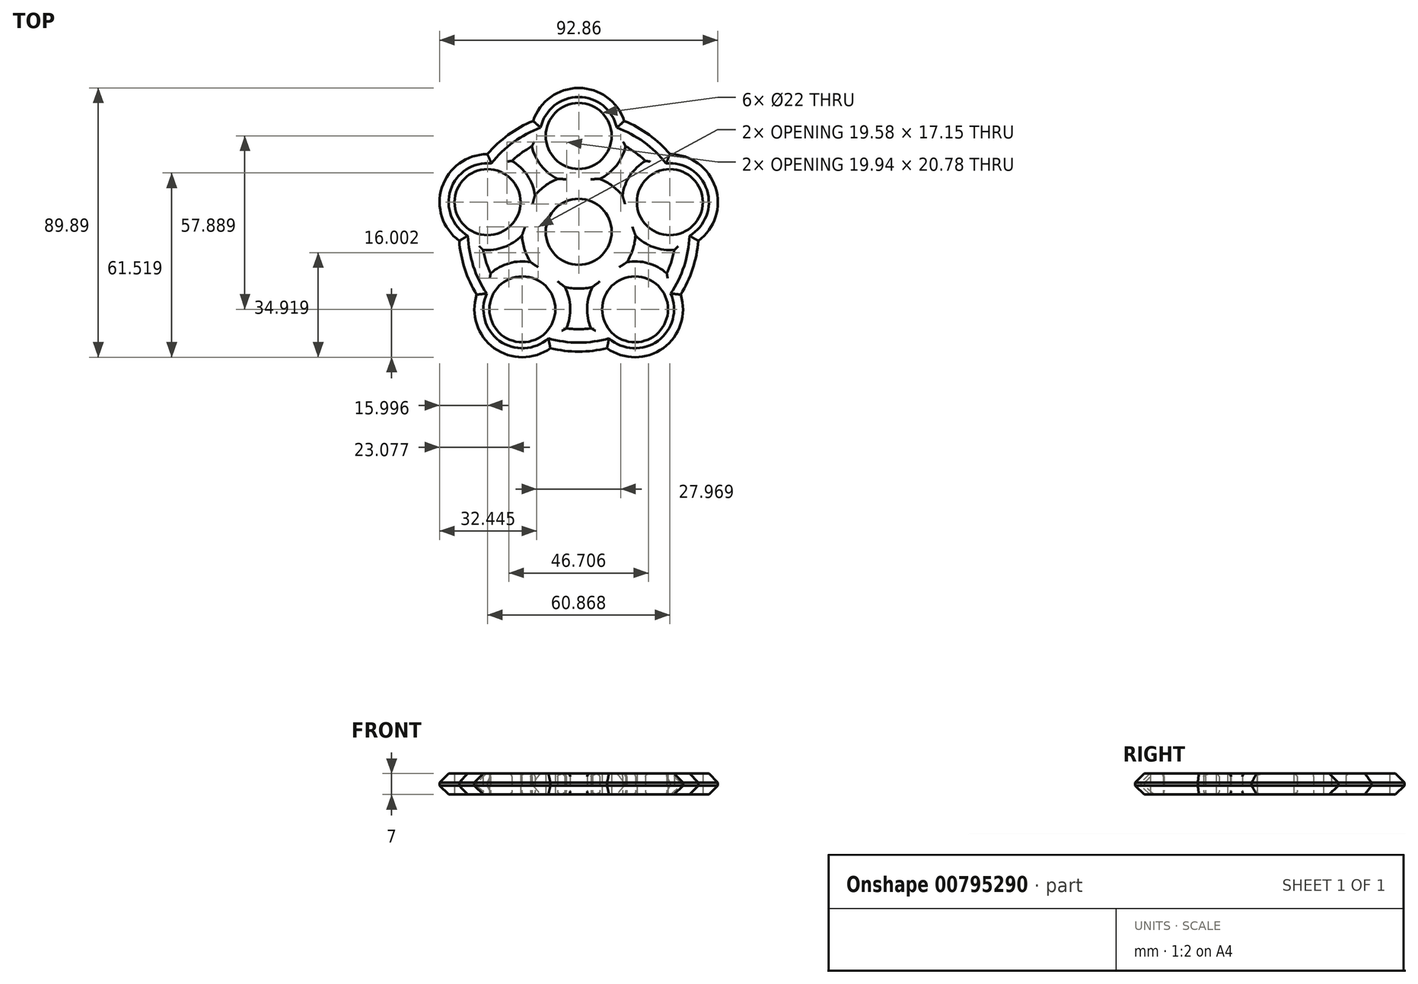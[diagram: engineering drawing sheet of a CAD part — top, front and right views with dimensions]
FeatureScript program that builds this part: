
annotation { "Feature Type Name" : "Feature", "Feature Type Description" : "" }
export const myFeature = defineFeature(function(context is Context, id is Id, definition is map)
    precondition{}
    {
        {
            var Q0;
            Q0=qCreatedBy(makeId("Top.planeOp"),FACE);
            var sketch = newSketch(context, id + "F0", { "sketchPlane" : qUnion([Q0])});
            skCircle(sketch, "E0", {"center": v(0, 0) * mm, "radius": 11 * mm});
            skCircle(sketch, "E1", {"center": v(0, 0) * mm, "radius": 19 * mm});
            skCircle(sketch, "E2", {"center": v(0, 0) * mm, "radius": 40 * mm});
            skCircle(sketch, "E3", {"center": v(0, 0) * mm, "radius": 32.5 * mm});
            skCircle(sketch, "E4", {"center": v(0, 32) * mm, "radius": 11 * mm});
            skCircle(sketch, "E5", {"center": v(0, 32) * mm, "radius": 16 * mm});
            skCircle(sketch, "E6.1.0", {"center": v(-30.43, 9.89) * mm, "radius": 16 * mm});
            skCircle(sketch, "E6.1.1", {"center": v(-30.43, 9.89) * mm, "radius": 11 * mm});
            skCircle(sketch, "E6.2.0", {"center": v(-18.8, -25.89) * mm, "radius": 16 * mm});
            skCircle(sketch, "E6.2.1", {"center": v(-18.8, -25.89) * mm, "radius": 11 * mm});
            skCircle(sketch, "E7.1.3.0", {"center": v(18.8, -25.89) * mm, "radius": 16 * mm});
            skCircle(sketch, "E7.2.3.0", {"center": v(18.8, -25.89) * mm, "radius": 11 * mm});
            skCircle(sketch, "E7.1.4.0", {"center": v(30.43, 9.89) * mm, "radius": 16 * mm});
            skCircle(sketch, "E7.2.4.0", {"center": v(30.43, 9.89) * mm, "radius": 11 * mm});
            skSolve(sketch);
        }
        {
            var Q0;
            {var subQ0=sQuery(id+"F0.wireOp",EDGE,"E6.1.0");var subQ1=sQuery(id+"F0.wireOp",EDGE,"E2");var subQ2=makeQuery(id+"F0.imprint","INTERSECT",VERTEX,{"disambiguationData":[OD(0.0)],"derivedFrom":[subQ1,subQ0]});Q0=makeQuery(id+"F0.imprint","IMPRINT",FACE,{"disambiguationData":[TD([[makeQuery(id+"F0.imprint","IMPRINT",EDGE,{"disambiguationData":[TD([[subQ2,-1.0]])],"derivedFrom":subQ1}),1.0]])]});}
            var Q1;
            {var subQ0=sQuery(id+"F0.wireOp",EDGE,"E6.1.0");var subQ1=sQuery(id+"F0.wireOp",EDGE,"E2");var subQ2=makeQuery(id+"F0.imprint","INTERSECT",VERTEX,{"disambiguationData":[OD(1.0)],"derivedFrom":[subQ1,subQ0]});Q1=makeQuery(id+"F0.imprint","IMPRINT",FACE,{"disambiguationData":[TD([[makeQuery(id+"F0.imprint","IMPRINT",EDGE,{"disambiguationData":[TD([[subQ2,1.0]])],"derivedFrom":subQ1}),1.0]])]});}
            var Q2;
            {var subQ0=sQuery(id+"F0.wireOp",EDGE,"E6.1.0");var subQ1=sQuery(id+"F0.wireOp",EDGE,"E2");var subQ2=makeQuery(id+"F0.imprint","INTERSECT",VERTEX,{"disambiguationData":[OD(1.0)],"derivedFrom":[subQ1,subQ0]});Q2=makeQuery(id+"F0.imprint","IMPRINT",FACE,{"disambiguationData":[TD([[makeQuery(id+"F0.imprint","IMPRINT",EDGE,{"disambiguationData":[TD([[subQ2,-1.0]])],"derivedFrom":subQ1}),1.0]])]});}
            var Q3;
            {var subQ0=sQuery(id+"F0.wireOp",EDGE,"E6.1.0");var subQ1=sQuery(id+"F0.wireOp",EDGE,"E2");var subQ2=makeQuery(id+"F0.imprint","INTERSECT",VERTEX,{"disambiguationData":[OD(0.0)],"derivedFrom":[subQ1,subQ0]});Q3=makeQuery(id+"F0.imprint","IMPRINT",FACE,{"disambiguationData":[TD([[makeQuery(id+"F0.imprint","IMPRINT",EDGE,{"disambiguationData":[TD([[subQ2,-1.0]])],"derivedFrom":subQ1}),-1.0]])]});}
            var Q4;
            {var subQ3=sQuery(id+"F0.wireOp",EDGE,"E6.1.0");var subQ5=sQuery(id+"F0.wireOp",EDGE,"E1");var subQ6=makeQuery(id+"F0.imprint","INTERSECT",VERTEX,{"disambiguationData":[OD(0.0)],"derivedFrom":[subQ5,subQ3]});Q4=makeQuery(id+"F0.imprint","IMPRINT",FACE,{"disambiguationData":[TD([[makeQuery(id+"F0.imprint","IMPRINT",EDGE,{"disambiguationData":[TD([[subQ6,-1.0]])],"derivedFrom":subQ5}),-1.0]])]});}
            var Q5;
            {var subQ0=sQuery(id+"F0.wireOp",EDGE,"E6.1.0");var subQ1=sQuery(id+"F0.wireOp",EDGE,"E1");var subQ2=makeQuery(id+"F0.imprint","INTERSECT",VERTEX,{"disambiguationData":[OD(0.0)],"derivedFrom":[subQ1,subQ0]});Q5=makeQuery(id+"F0.imprint","IMPRINT",FACE,{"disambiguationData":[TD([[makeQuery(id+"F0.imprint","IMPRINT",EDGE,{"disambiguationData":[TD([[subQ2,-1.0]])],"derivedFrom":subQ1}),1.0]])]});}
            var Q6;
            Q6=makeQuery(id+"F0.imprint","IMPRINT",FACE,{"disambiguationData":[TD([[makeQuery(id+"F0.imprint","IMPRINT",EDGE,{"derivedFrom":sQuery(id+"F0.wireOp",EDGE,"E0")}),-1.0]])]});
            var Q7;
            {var subQ0=sQuery(id+"F0.wireOp",EDGE,"E6.2.0");var subQ1=sQuery(id+"F0.wireOp",EDGE,"E1");var subQ2=makeQuery(id+"F0.imprint","INTERSECT",VERTEX,{"disambiguationData":[OD(0.0)],"derivedFrom":[subQ1,subQ0]});Q7=makeQuery(id+"F0.imprint","IMPRINT",FACE,{"disambiguationData":[TD([[makeQuery(id+"F0.imprint","IMPRINT",EDGE,{"disambiguationData":[TD([[subQ2,-1.0]])],"derivedFrom":subQ1}),1.0]])]});}
            var Q8;
            {var subQ0=sQuery(id+"F0.wireOp",EDGE,"E6.2.0");var subQ1=sQuery(id+"F0.wireOp",EDGE,"E1");var subQ9=makeQuery(id+"F0.imprint","INTERSECT",VERTEX,{"disambiguationData":[OD(0.0)],"derivedFrom":[subQ1,subQ0]});Q8=makeQuery(id+"F0.imprint","IMPRINT",FACE,{"disambiguationData":[TD([[makeQuery(id+"F0.imprint","IMPRINT",EDGE,{"disambiguationData":[TD([[subQ9,-1.0]])],"derivedFrom":subQ1}),-1.0]])]});}
            var Q9;
            {var subQ0=sQuery(id+"F0.wireOp",EDGE,"E6.2.0");var subQ1=sQuery(id+"F0.wireOp",EDGE,"E2");var subQ2=makeQuery(id+"F0.imprint","INTERSECT",VERTEX,{"disambiguationData":[OD(0.0)],"derivedFrom":[subQ1,subQ0]});Q9=makeQuery(id+"F0.imprint","IMPRINT",FACE,{"disambiguationData":[TD([[makeQuery(id+"F0.imprint","IMPRINT",EDGE,{"disambiguationData":[TD([[subQ2,-1.0]])],"derivedFrom":subQ1}),1.0]])]});}
            var Q10;
            {var subQ0=sQuery(id+"F0.wireOp",EDGE,"E6.2.0");var subQ1=sQuery(id+"F0.wireOp",EDGE,"E2");var subQ2=makeQuery(id+"F0.imprint","INTERSECT",VERTEX,{"disambiguationData":[OD(1.0)],"derivedFrom":[subQ1,subQ0]});Q10=makeQuery(id+"F0.imprint","IMPRINT",FACE,{"disambiguationData":[TD([[makeQuery(id+"F0.imprint","IMPRINT",EDGE,{"disambiguationData":[TD([[subQ2,1.0]])],"derivedFrom":subQ1}),1.0]])]});}
            var Q11;
            {var subQ0=sQuery(id+"F0.wireOp",EDGE,"E5");var subQ1=sQuery(id+"F0.wireOp",EDGE,"E2");var subQ2=makeQuery(id+"F0.imprint","INTERSECT",VERTEX,{"disambiguationData":[OD(0.0)],"derivedFrom":[subQ1,subQ0]});Q11=makeQuery(id+"F0.imprint","IMPRINT",FACE,{"disambiguationData":[TD([[makeQuery(id+"F0.imprint","IMPRINT",EDGE,{"disambiguationData":[TD([[subQ2,1.0]])],"derivedFrom":subQ1}),1.0]])]});}
            var Q12;
            {var subQ0=sQuery(id+"F0.wireOp",EDGE,"E6.2.0");var subQ1=sQuery(id+"F0.wireOp",EDGE,"E2");var subQ2=makeQuery(id+"F0.imprint","INTERSECT",VERTEX,{"disambiguationData":[OD(0.0)],"derivedFrom":[subQ1,subQ0]});Q12=makeQuery(id+"F0.imprint","IMPRINT",FACE,{"disambiguationData":[TD([[makeQuery(id+"F0.imprint","IMPRINT",EDGE,{"disambiguationData":[TD([[subQ2,-1.0]])],"derivedFrom":subQ1}),-1.0]])]});}
            var Q13;
            {var subQ0=sQuery(id+"F0.wireOp",EDGE,"E5");var subQ1=sQuery(id+"F0.wireOp",EDGE,"E1");var subQ2=makeQuery(id+"F0.imprint","INTERSECT",VERTEX,{"disambiguationData":[OD(0.0)],"derivedFrom":[subQ1,subQ0]});Q13=makeQuery(id+"F0.imprint","IMPRINT",FACE,{"disambiguationData":[TD([[makeQuery(id+"F0.imprint","IMPRINT",EDGE,{"disambiguationData":[TD([[subQ2,1.0]])],"derivedFrom":subQ1}),1.0]])]});}
            var Q14;
            {var subQ0=sQuery(id+"F0.wireOp",EDGE,"E5");var subQ1=sQuery(id+"F0.wireOp",EDGE,"E2");var subQ2=makeQuery(id+"F0.imprint","INTERSECT",VERTEX,{"disambiguationData":[OD(1.0)],"derivedFrom":[subQ1,subQ0]});Q14=makeQuery(id+"F0.imprint","IMPRINT",FACE,{"disambiguationData":[TD([[makeQuery(id+"F0.imprint","IMPRINT",EDGE,{"disambiguationData":[TD([[subQ2,-1.0]])],"derivedFrom":subQ1}),1.0]])]});}
            var Q15;
            {var subQ0=sQuery(id+"F0.wireOp",EDGE,"E5");var subQ1=sQuery(id+"F0.wireOp",EDGE,"E2");var subQ2=makeQuery(id+"F0.imprint","INTERSECT",VERTEX,{"disambiguationData":[OD(0.0)],"derivedFrom":[subQ1,subQ0]});Q15=makeQuery(id+"F0.imprint","IMPRINT",FACE,{"disambiguationData":[TD([[makeQuery(id+"F0.imprint","IMPRINT",EDGE,{"disambiguationData":[TD([[subQ2,-1.0]])],"derivedFrom":subQ1}),1.0]])]});}
            var Q16;
            {var subQ0=sQuery(id+"F0.wireOp",EDGE,"E5");var subQ1=sQuery(id+"F0.wireOp",EDGE,"E2");var subQ2=makeQuery(id+"F0.imprint","INTERSECT",VERTEX,{"disambiguationData":[OD(1.0)],"derivedFrom":[subQ1,subQ0]});Q16=makeQuery(id+"F0.imprint","IMPRINT",FACE,{"disambiguationData":[TD([[makeQuery(id+"F0.imprint","IMPRINT",EDGE,{"disambiguationData":[TD([[subQ2,1.0]])],"derivedFrom":subQ1}),1.0]])]});}
            var Q17;
            {var subQ0=sQuery(id+"F0.wireOp",EDGE,"E5");var subQ1=sQuery(id+"F0.wireOp",EDGE,"E2");var subQ2=makeQuery(id+"F0.imprint","INTERSECT",VERTEX,{"disambiguationData":[OD(0.0)],"derivedFrom":[subQ1,subQ0]});Q17=makeQuery(id+"F0.imprint","IMPRINT",FACE,{"disambiguationData":[TD([[makeQuery(id+"F0.imprint","IMPRINT",EDGE,{"disambiguationData":[TD([[subQ2,-1.0]])],"derivedFrom":subQ1}),-1.0]])]});}
            var Q18;
            {var subQ0=sQuery(id+"F0.wireOp",EDGE,"e3311fa9-2675-4763-9959-c69614a33db8.1.3.0");var subQ1=sQuery(id+"F0.wireOp",EDGE,"E1");var subQ2=makeQuery(id+"F0.imprint","INTERSECT",VERTEX,{"disambiguationData":[OD(0.0)],"derivedFrom":[subQ1,subQ0]});Q18=makeQuery(id+"F0.imprint","IMPRINT",FACE,{"disambiguationData":[TD([[makeQuery(id+"F0.imprint","IMPRINT",EDGE,{"disambiguationData":[TD([[subQ2,1.0]])],"derivedFrom":subQ1}),1.0]])]});}
            var Q19;
            {var subQ0=sQuery(id+"F0.wireOp",EDGE,"e3311fa9-2675-4763-9959-c69614a33db8.1.3.0");var subQ7=sQuery(id+"F0.wireOp",EDGE,"E1");var subQ8=makeQuery(id+"F0.imprint","INTERSECT",VERTEX,{"disambiguationData":[OD(0.0)],"derivedFrom":[subQ7,subQ0]});Q19=makeQuery(id+"F0.imprint","IMPRINT",FACE,{"disambiguationData":[TD([[makeQuery(id+"F0.imprint","IMPRINT",EDGE,{"disambiguationData":[TD([[subQ8,1.0]])],"derivedFrom":subQ7}),-1.0]])]});}
            var Q20;
            {var subQ0=sQuery(id+"F0.wireOp",EDGE,"e3311fa9-2675-4763-9959-c69614a33db8.1.3.0");var subQ1=sQuery(id+"F0.wireOp",EDGE,"E2");var subQ2=makeQuery(id+"F0.imprint","INTERSECT",VERTEX,{"disambiguationData":[OD(1.0)],"derivedFrom":[subQ1,subQ0]});Q20=makeQuery(id+"F0.imprint","IMPRINT",FACE,{"disambiguationData":[TD([[makeQuery(id+"F0.imprint","IMPRINT",EDGE,{"disambiguationData":[TD([[subQ2,-1.0]])],"derivedFrom":subQ1}),1.0]])]});}
            var Q21;
            {var subQ0=sQuery(id+"F0.wireOp",EDGE,"e3311fa9-2675-4763-9959-c69614a33db8.1.3.0");var subQ1=sQuery(id+"F0.wireOp",EDGE,"E2");var subQ2=makeQuery(id+"F0.imprint","INTERSECT",VERTEX,{"disambiguationData":[OD(0.0)],"derivedFrom":[subQ1,subQ0]});Q21=makeQuery(id+"F0.imprint","IMPRINT",FACE,{"disambiguationData":[TD([[makeQuery(id+"F0.imprint","IMPRINT",EDGE,{"disambiguationData":[TD([[subQ2,1.0]])],"derivedFrom":subQ1}),1.0]])]});}
            var Q22;
            {var subQ0=sQuery(id+"F0.wireOp",EDGE,"e3311fa9-2675-4763-9959-c69614a33db8.1.3.0");var subQ1=sQuery(id+"F0.wireOp",EDGE,"E2");var subQ2=makeQuery(id+"F0.imprint","INTERSECT",VERTEX,{"disambiguationData":[OD(0.0)],"derivedFrom":[subQ1,subQ0]});Q22=makeQuery(id+"F0.imprint","IMPRINT",FACE,{"disambiguationData":[TD([[makeQuery(id+"F0.imprint","IMPRINT",EDGE,{"disambiguationData":[TD([[subQ2,1.0]])],"derivedFrom":subQ1}),-1.0]])]});}
            var Q23;
            {var subQ0=sQuery(id+"F0.wireOp",EDGE,"E6.2.0");var subQ1=sQuery(id+"F0.wireOp",EDGE,"E2");var subQ2=makeQuery(id+"F0.imprint","INTERSECT",VERTEX,{"disambiguationData":[OD(1.0)],"derivedFrom":[subQ1,subQ0]});Q23=makeQuery(id+"F0.imprint","IMPRINT",FACE,{"disambiguationData":[TD([[makeQuery(id+"F0.imprint","IMPRINT",EDGE,{"disambiguationData":[TD([[subQ2,-1.0]])],"derivedFrom":subQ1}),1.0]])]});}
            var Q24;
            {var subQ3=sQuery(id+"F0.wireOp",EDGE,"E5");var subQ5=sQuery(id+"F0.wireOp",EDGE,"E1");var subQ6=makeQuery(id+"F0.imprint","INTERSECT",VERTEX,{"disambiguationData":[OD(0.0)],"derivedFrom":[subQ5,subQ3]});Q24=makeQuery(id+"F0.imprint","IMPRINT",FACE,{"disambiguationData":[TD([[makeQuery(id+"F0.imprint","IMPRINT",EDGE,{"disambiguationData":[TD([[subQ6,-1.0]])],"derivedFrom":subQ5}),-1.0]])]});}
            var Q25;
            {var subQ0=sQuery(id+"F0.wireOp",EDGE,"E5");var subQ1=sQuery(id+"F0.wireOp",EDGE,"E1");var subQ2=makeQuery(id+"F0.imprint","INTERSECT",VERTEX,{"disambiguationData":[OD(0.0)],"derivedFrom":[subQ1,subQ0]});Q25=makeQuery(id+"F0.imprint","IMPRINT",FACE,{"disambiguationData":[TD([[makeQuery(id+"F0.imprint","IMPRINT",EDGE,{"disambiguationData":[TD([[subQ2,-1.0]])],"derivedFrom":subQ1}),1.0]])]});}
            var Q26;
            {var subQ0=sQuery(id+"F0.wireOp",EDGE,"E7.1.4.0");var subQ1=sQuery(id+"F0.wireOp",EDGE,"E1");var subQ2=makeQuery(id+"F0.imprint","INTERSECT",VERTEX,{"disambiguationData":[OD(0.0)],"derivedFrom":[subQ1,subQ0]});Q26=makeQuery(id+"F0.imprint","IMPRINT",FACE,{"disambiguationData":[TD([[makeQuery(id+"F0.imprint","IMPRINT",EDGE,{"disambiguationData":[TD([[subQ2,1.0]])],"derivedFrom":subQ1}),1.0]])]});}
            var Q27;
            {var subQ0=sQuery(id+"F0.wireOp",EDGE,"E7.1.4.0");var subQ1=sQuery(id+"F0.wireOp",EDGE,"E1");var subQ2=makeQuery(id+"F0.imprint","INTERSECT",VERTEX,{"disambiguationData":[OD(0.0)],"derivedFrom":[subQ1,subQ0]});Q27=makeQuery(id+"F0.imprint","IMPRINT",FACE,{"disambiguationData":[TD([[makeQuery(id+"F0.imprint","IMPRINT",EDGE,{"disambiguationData":[TD([[subQ2,1.0]])],"derivedFrom":subQ1}),-1.0]])]});}
            var Q28;
            {var subQ0=sQuery(id+"F0.wireOp",EDGE,"E7.1.4.0");var subQ1=sQuery(id+"F0.wireOp",EDGE,"E2");var subQ2=makeQuery(id+"F0.imprint","INTERSECT",VERTEX,{"disambiguationData":[OD(0.0)],"derivedFrom":[subQ1,subQ0]});Q28=makeQuery(id+"F0.imprint","IMPRINT",FACE,{"disambiguationData":[TD([[makeQuery(id+"F0.imprint","IMPRINT",EDGE,{"disambiguationData":[TD([[subQ2,1.0]])],"derivedFrom":subQ1}),1.0]])]});}
            var Q29;
            {var subQ0=sQuery(id+"F0.wireOp",EDGE,"E7.1.4.0");var subQ1=sQuery(id+"F0.wireOp",EDGE,"E2");var subQ2=makeQuery(id+"F0.imprint","INTERSECT",VERTEX,{"disambiguationData":[OD(0.0)],"derivedFrom":[subQ1,subQ0]});Q29=makeQuery(id+"F0.imprint","IMPRINT",FACE,{"disambiguationData":[TD([[makeQuery(id+"F0.imprint","IMPRINT",EDGE,{"disambiguationData":[TD([[subQ2,1.0]])],"derivedFrom":subQ1}),-1.0]])]});}
            var Q30;
            {var subQ0=sQuery(id+"F0.wireOp",EDGE,"E7.1.4.0");var subQ1=sQuery(id+"F0.wireOp",EDGE,"E2");var subQ2=makeQuery(id+"F0.imprint","INTERSECT",VERTEX,{"disambiguationData":[OD(1.0)],"derivedFrom":[subQ1,subQ0]});Q30=makeQuery(id+"F0.imprint","IMPRINT",FACE,{"disambiguationData":[TD([[makeQuery(id+"F0.imprint","IMPRINT",EDGE,{"disambiguationData":[TD([[subQ2,-1.0]])],"derivedFrom":subQ1}),1.0]])]});}
            var Q31;
            {var subQ3=sQuery(id+"F0.wireOp",EDGE,"E7.1.3.0");var subQ7=sQuery(id+"F0.wireOp",EDGE,"E1");var subQ9=makeQuery(id+"F0.imprint","INTERSECT",VERTEX,{"disambiguationData":[OD(0.0)],"derivedFrom":[subQ7,subQ3]});Q31=makeQuery(id+"F0.imprint","IMPRINT",FACE,{"disambiguationData":[TD([[makeQuery(id+"F0.imprint","IMPRINT",EDGE,{"disambiguationData":[TD([[subQ9,-1.0]])],"derivedFrom":subQ7}),-1.0]])]});}
            var Q32;
            {var subQ0=sQuery(id+"F0.wireOp",EDGE,"E7.1.3.0");var subQ1=sQuery(id+"F0.wireOp",EDGE,"E1");var subQ2=makeQuery(id+"F0.imprint","INTERSECT",VERTEX,{"disambiguationData":[OD(0.0)],"derivedFrom":[subQ1,subQ0]});Q32=makeQuery(id+"F0.imprint","IMPRINT",FACE,{"disambiguationData":[TD([[makeQuery(id+"F0.imprint","IMPRINT",EDGE,{"disambiguationData":[TD([[subQ2,-1.0]])],"derivedFrom":subQ1}),1.0]])]});}
            var Q33;
            {var subQ0=sQuery(id+"F0.wireOp",EDGE,"E7.1.3.0");var subQ1=sQuery(id+"F0.wireOp",EDGE,"E2");var subQ2=makeQuery(id+"F0.imprint","INTERSECT",VERTEX,{"disambiguationData":[OD(0.0)],"derivedFrom":[subQ1,subQ0]});Q33=makeQuery(id+"F0.imprint","IMPRINT",FACE,{"disambiguationData":[TD([[makeQuery(id+"F0.imprint","IMPRINT",EDGE,{"disambiguationData":[TD([[subQ2,-1.0]])],"derivedFrom":subQ1}),1.0]])]});}
            var Q34;
            {var subQ0=sQuery(id+"F0.wireOp",EDGE,"E7.1.3.0");var subQ1=sQuery(id+"F0.wireOp",EDGE,"E2");var subQ2=makeQuery(id+"F0.imprint","INTERSECT",VERTEX,{"disambiguationData":[OD(0.0)],"derivedFrom":[subQ1,subQ0]});Q34=makeQuery(id+"F0.imprint","IMPRINT",FACE,{"disambiguationData":[TD([[makeQuery(id+"F0.imprint","IMPRINT",EDGE,{"disambiguationData":[TD([[subQ2,-1.0]])],"derivedFrom":subQ1}),-1.0]])]});}
            var Q35;
            {var subQ0=sQuery(id+"F0.wireOp",EDGE,"E7.1.3.0");var subQ1=sQuery(id+"F0.wireOp",EDGE,"E2");var subQ2=makeQuery(id+"F0.imprint","INTERSECT",VERTEX,{"disambiguationData":[OD(1.0)],"derivedFrom":[subQ1,subQ0]});Q35=makeQuery(id+"F0.imprint","IMPRINT",FACE,{"disambiguationData":[TD([[makeQuery(id+"F0.imprint","IMPRINT",EDGE,{"disambiguationData":[TD([[subQ2,1.0]])],"derivedFrom":subQ1}),1.0]])]});}
            var Q36;
            {var subQ0=sQuery(id+"F0.wireOp",EDGE,"E7.1.3.0");var subQ1=sQuery(id+"F0.wireOp",EDGE,"E2");var subQ2=makeQuery(id+"F0.imprint","INTERSECT",VERTEX,{"disambiguationData":[OD(1.0)],"derivedFrom":[subQ1,subQ0]});Q36=makeQuery(id+"F0.imprint","IMPRINT",FACE,{"disambiguationData":[TD([[makeQuery(id+"F0.imprint","IMPRINT",EDGE,{"disambiguationData":[TD([[subQ2,-1.0]])],"derivedFrom":subQ1}),1.0]])]});}
            extrude(context, id + "F1", {"entities" : qUnion([Q0, Q1, Q2, Q3, Q4, Q5, Q6, Q7, Q8, Q9, Q10, Q11, Q12, Q13, Q14, Q15, Q16, Q17, Q18, Q19, Q20, Q21, Q22, Q23, Q24, Q25, Q26, Q27, Q28, Q29, Q30, Q31, Q32, Q33, Q34, Q35, Q36]), "depth" : 7 * mm, "offsetDistance" : 25 * mm});
        }
        {
            var Q0;
            {var subQ0=sQuery(id+"F0.wireOp",EDGE,"E2");Q0=makeQuery(id+"F1.opExtrude","CAP_EDGE",EDGE,{"disambiguationData":[OSD([subQ0]),TDD([makeQuery(id+"F0.imprint","IMPRINT",EDGE,{"disambiguationData":[TD([[makeQuery(id+"F0.imprint","INTERSECT",VERTEX,{"disambiguationData":[OD(1.0)],"derivedFrom":[subQ0,sQuery(id+"F0.wireOp",EDGE,"E6.1.0")]}),-1.0]])],"derivedFrom":subQ0})])],"isStart":false});}
            var Q1;
            {var subQ0=sQuery(id+"F0.wireOp",EDGE,"E2");Q1=makeQuery(id+"F1.opExtrude","CAP_EDGE",EDGE,{"disambiguationData":[OSD([subQ0]),TDD([makeQuery(id+"F0.imprint","IMPRINT",EDGE,{"disambiguationData":[TD([[makeQuery(id+"F0.imprint","INTERSECT",VERTEX,{"disambiguationData":[OD(1.0)],"derivedFrom":[subQ0,sQuery(id+"F0.wireOp",EDGE,"E5")]}),-1.0]])],"derivedFrom":subQ0})])],"isStart":false});}
            var Q2;
            {var subQ0=sQuery(id+"F0.wireOp",EDGE,"E6.1.0");var subQ1=sQuery(id+"F0.wireOp",EDGE,"E2");Q2=makeQuery(id+"F1.opExtrude","CAP_EDGE",EDGE,{"disambiguationData":[OSD([subQ0]),TDD([makeQuery(id+"F0.imprint","IMPRINT",EDGE,{"disambiguationData":[TD([[makeQuery(id+"F0.imprint","INTERSECT",VERTEX,{"disambiguationData":[OD(0.0)],"derivedFrom":[subQ1,subQ0]}),-1.0]])],"derivedFrom":subQ0})])],"isStart":false});}
            var Q3;
            {var subQ0=sQuery(id+"F0.wireOp",EDGE,"E5");var subQ1=sQuery(id+"F0.wireOp",EDGE,"E2");Q3=makeQuery(id+"F1.opExtrude","CAP_EDGE",EDGE,{"disambiguationData":[OSD([subQ0]),TDD([makeQuery(id+"F0.imprint","IMPRINT",EDGE,{"disambiguationData":[TD([[makeQuery(id+"F0.imprint","INTERSECT",VERTEX,{"disambiguationData":[OD(0.0)],"derivedFrom":[subQ1,subQ0]}),-1.0]])],"derivedFrom":subQ0})])],"isStart":false});}
            var Q4;
            {var subQ0=sQuery(id+"F0.wireOp",EDGE,"E6.2.0");var subQ1=sQuery(id+"F0.wireOp",EDGE,"E2");Q4=makeQuery(id+"F1.opExtrude","CAP_EDGE",EDGE,{"disambiguationData":[OSD([subQ0]),TDD([makeQuery(id+"F0.imprint","IMPRINT",EDGE,{"disambiguationData":[TD([[makeQuery(id+"F0.imprint","INTERSECT",VERTEX,{"disambiguationData":[OD(0.0)],"derivedFrom":[subQ1,subQ0]}),-1.0]])],"derivedFrom":subQ0})])],"isStart":false});}
            var Q5;
            {var subQ0=sQuery(id+"F0.wireOp",EDGE,"E2");Q5=makeQuery(id+"F1.opExtrude","CAP_EDGE",EDGE,{"disambiguationData":[OSD([subQ0]),TDD([makeQuery(id+"F0.imprint","IMPRINT",EDGE,{"disambiguationData":[TD([[makeQuery(id+"F0.imprint","INTERSECT",VERTEX,{"disambiguationData":[OD(0.0)],"derivedFrom":[subQ0,sQuery(id+"F0.wireOp",EDGE,"E5")]}),1.0]])],"derivedFrom":subQ0})])],"isStart":false});}
            var Q6;
            {var subQ0=sQuery(id+"F0.wireOp",EDGE,"E2");Q6=makeQuery(id+"F1.opExtrude","CAP_EDGE",EDGE,{"disambiguationData":[OSD([subQ0]),TDD([makeQuery(id+"F0.imprint","IMPRINT",EDGE,{"disambiguationData":[TD([[makeQuery(id+"F0.imprint","INTERSECT",VERTEX,{"disambiguationData":[OD(0.0)],"derivedFrom":[subQ0,sQuery(id+"F0.wireOp",EDGE,"E5")]}),1.0]])],"derivedFrom":subQ0})])],"isStart":true});}
            var Q7;
            {var subQ0=sQuery(id+"F0.wireOp",EDGE,"E6.2.0");var subQ1=sQuery(id+"F0.wireOp",EDGE,"E2");Q7=makeQuery(id+"F1.opExtrude","CAP_EDGE",EDGE,{"disambiguationData":[OSD([subQ0]),TDD([makeQuery(id+"F0.imprint","IMPRINT",EDGE,{"disambiguationData":[TD([[makeQuery(id+"F0.imprint","INTERSECT",VERTEX,{"disambiguationData":[OD(0.0)],"derivedFrom":[subQ1,subQ0]}),-1.0]])],"derivedFrom":subQ0})])],"isStart":true});}
            var Q8;
            {var subQ0=sQuery(id+"F0.wireOp",EDGE,"E2");Q8=makeQuery(id+"F1.opExtrude","CAP_EDGE",EDGE,{"disambiguationData":[OSD([subQ0]),TDD([makeQuery(id+"F0.imprint","IMPRINT",EDGE,{"disambiguationData":[TD([[makeQuery(id+"F0.imprint","INTERSECT",VERTEX,{"disambiguationData":[OD(1.0)],"derivedFrom":[subQ0,sQuery(id+"F0.wireOp",EDGE,"E6.1.0")]}),-1.0]])],"derivedFrom":subQ0})])],"isStart":true});}
            var Q9;
            {var subQ0=sQuery(id+"F0.wireOp",EDGE,"E6.1.0");var subQ1=sQuery(id+"F0.wireOp",EDGE,"E2");Q9=makeQuery(id+"F1.opExtrude","CAP_EDGE",EDGE,{"disambiguationData":[OSD([subQ0]),TDD([makeQuery(id+"F0.imprint","IMPRINT",EDGE,{"disambiguationData":[TD([[makeQuery(id+"F0.imprint","INTERSECT",VERTEX,{"disambiguationData":[OD(0.0)],"derivedFrom":[subQ1,subQ0]}),-1.0]])],"derivedFrom":subQ0})])],"isStart":true});}
            var Q10;
            {var subQ0=sQuery(id+"F0.wireOp",EDGE,"E2");Q10=makeQuery(id+"F1.opExtrude","CAP_EDGE",EDGE,{"disambiguationData":[OSD([subQ0]),TDD([makeQuery(id+"F0.imprint","IMPRINT",EDGE,{"disambiguationData":[TD([[makeQuery(id+"F0.imprint","INTERSECT",VERTEX,{"disambiguationData":[OD(1.0)],"derivedFrom":[subQ0,sQuery(id+"F0.wireOp",EDGE,"E5")]}),-1.0]])],"derivedFrom":subQ0})])],"isStart":true});}
            var Q11;
            {var subQ0=sQuery(id+"F0.wireOp",EDGE,"E5");var subQ1=sQuery(id+"F0.wireOp",EDGE,"E2");Q11=makeQuery(id+"F1.opExtrude","CAP_EDGE",EDGE,{"disambiguationData":[OSD([subQ0]),TDD([makeQuery(id+"F0.imprint","IMPRINT",EDGE,{"disambiguationData":[TD([[makeQuery(id+"F0.imprint","INTERSECT",VERTEX,{"disambiguationData":[OD(0.0)],"derivedFrom":[subQ1,subQ0]}),-1.0]])],"derivedFrom":subQ0})])],"isStart":true});}
            var Q12;
            {var subQ0=sQuery(id+"F0.wireOp",EDGE,"E2");Q12=makeQuery(id+"F1.opExtrude","CAP_EDGE",EDGE,{"disambiguationData":[OSD([subQ0]),TDD([makeQuery(id+"F0.imprint","IMPRINT",EDGE,{"disambiguationData":[TD([[makeQuery(id+"F0.imprint","INTERSECT",VERTEX,{"disambiguationData":[OD(1.0)],"derivedFrom":[subQ0,sQuery(id+"F0.wireOp",EDGE,"E6.2.0")]}),-1.0]])],"derivedFrom":subQ0})])],"isStart":false});}
            var Q13;
            {var subQ0=sQuery(id+"F0.wireOp",EDGE,"E2");Q13=makeQuery(id+"F1.opExtrude","CAP_EDGE",EDGE,{"disambiguationData":[OSD([subQ0]),TDD([makeQuery(id+"F0.imprint","IMPRINT",EDGE,{"disambiguationData":[TD([[makeQuery(id+"F0.imprint","INTERSECT",VERTEX,{"disambiguationData":[OD(1.0)],"derivedFrom":[subQ0,sQuery(id+"F0.wireOp",EDGE,"E6.2.0")]}),-1.0]])],"derivedFrom":subQ0})])],"isStart":true});}
            var Q14;
            {var subQ0=sQuery(id+"F0.wireOp",EDGE,"e3311fa9-2675-4763-9959-c69614a33db8.1.3.0");var subQ1=sQuery(id+"F0.wireOp",EDGE,"E2");Q14=makeQuery(id+"F1.opExtrude","CAP_EDGE",EDGE,{"disambiguationData":[OSD([subQ0]),TDD([makeQuery(id+"F0.imprint","IMPRINT",EDGE,{"disambiguationData":[TD([[makeQuery(id+"F0.imprint","INTERSECT",VERTEX,{"disambiguationData":[OD(0.0)],"derivedFrom":[subQ1,subQ0]}),1.0]])],"derivedFrom":subQ0})])],"isStart":false});}
            var Q15;
            {var subQ0=sQuery(id+"F0.wireOp",EDGE,"e3311fa9-2675-4763-9959-c69614a33db8.1.3.0");var subQ1=sQuery(id+"F0.wireOp",EDGE,"E2");Q15=makeQuery(id+"F1.opExtrude","CAP_EDGE",EDGE,{"disambiguationData":[OSD([subQ0]),TDD([makeQuery(id+"F0.imprint","IMPRINT",EDGE,{"disambiguationData":[TD([[makeQuery(id+"F0.imprint","INTERSECT",VERTEX,{"disambiguationData":[OD(0.0)],"derivedFrom":[subQ1,subQ0]}),1.0]])],"derivedFrom":subQ0})])],"isStart":true});}
            var Q16;
            {var subQ0=sQuery(id+"F0.wireOp",EDGE,"E7.1.3.0");var subQ1=sQuery(id+"F0.wireOp",EDGE,"E2");Q16=makeQuery(id+"F1.opExtrude","CAP_EDGE",EDGE,{"disambiguationData":[OSD([subQ0]),TDD([makeQuery(id+"F0.imprint","IMPRINT",EDGE,{"disambiguationData":[TD([[makeQuery(id+"F0.imprint","INTERSECT",VERTEX,{"disambiguationData":[OD(0.0)],"derivedFrom":[subQ1,subQ0]}),-1.0]])],"derivedFrom":subQ0})])],"isStart":false});}
            var Q17;
            {var subQ0=sQuery(id+"F0.wireOp",EDGE,"E2");Q17=makeQuery(id+"F1.opExtrude","CAP_EDGE",EDGE,{"disambiguationData":[OSD([subQ0]),TDD([makeQuery(id+"F0.imprint","IMPRINT",EDGE,{"disambiguationData":[TD([[makeQuery(id+"F0.imprint","INTERSECT",VERTEX,{"disambiguationData":[OD(1.0)],"derivedFrom":[subQ0,sQuery(id+"F0.wireOp",EDGE,"E7.1.3.0")]}),-1.0]])],"derivedFrom":subQ0})])],"isStart":false});}
            var Q18;
            {var subQ0=sQuery(id+"F0.wireOp",EDGE,"E7.1.4.0");var subQ1=sQuery(id+"F0.wireOp",EDGE,"E2");Q18=makeQuery(id+"F1.opExtrude","CAP_EDGE",EDGE,{"disambiguationData":[OSD([subQ0]),TDD([makeQuery(id+"F0.imprint","IMPRINT",EDGE,{"disambiguationData":[TD([[makeQuery(id+"F0.imprint","INTERSECT",VERTEX,{"disambiguationData":[OD(0.0)],"derivedFrom":[subQ1,subQ0]}),1.0]])],"derivedFrom":subQ0})])],"isStart":false});}
            var Q19;
            {var subQ0=sQuery(id+"F0.wireOp",EDGE,"E7.1.3.0");var subQ1=sQuery(id+"F0.wireOp",EDGE,"E2");Q19=makeQuery(id+"F1.opExtrude","CAP_EDGE",EDGE,{"disambiguationData":[OSD([subQ0]),TDD([makeQuery(id+"F0.imprint","IMPRINT",EDGE,{"disambiguationData":[TD([[makeQuery(id+"F0.imprint","INTERSECT",VERTEX,{"disambiguationData":[OD(0.0)],"derivedFrom":[subQ1,subQ0]}),-1.0]])],"derivedFrom":subQ0})])],"isStart":true});}
            var Q20;
            {var subQ0=sQuery(id+"F0.wireOp",EDGE,"E2");Q20=makeQuery(id+"F1.opExtrude","CAP_EDGE",EDGE,{"disambiguationData":[OSD([subQ0]),TDD([makeQuery(id+"F0.imprint","IMPRINT",EDGE,{"disambiguationData":[TD([[makeQuery(id+"F0.imprint","INTERSECT",VERTEX,{"disambiguationData":[OD(1.0)],"derivedFrom":[subQ0,sQuery(id+"F0.wireOp",EDGE,"E7.1.3.0")]}),-1.0]])],"derivedFrom":subQ0})])],"isStart":true});}
            var Q21;
            {var subQ0=sQuery(id+"F0.wireOp",EDGE,"E7.1.4.0");var subQ1=sQuery(id+"F0.wireOp",EDGE,"E2");Q21=makeQuery(id+"F1.opExtrude","CAP_EDGE",EDGE,{"disambiguationData":[OSD([subQ0]),TDD([makeQuery(id+"F0.imprint","IMPRINT",EDGE,{"disambiguationData":[TD([[makeQuery(id+"F0.imprint","INTERSECT",VERTEX,{"disambiguationData":[OD(0.0)],"derivedFrom":[subQ1,subQ0]}),1.0]])],"derivedFrom":subQ0})])],"isStart":true});}
            chamfer(context, id + "F2", {"entities" : qUnion([Q0, Q1, Q2, Q3, Q4, Q5, Q6, Q7, Q8, Q9, Q10, Q11, Q12, Q13, Q14, Q15, Q16, Q17, Q18, Q19, Q20, Q21]), "width" : 3 * mm, "tangentPropagation" : true});
        }
        {
            var Q0;
            {var subQ0=sQuery(id+"F0.wireOp",EDGE,"E3");Q0=makeQuery(id+"F1.opExtrude","CAP_EDGE",EDGE,{"disambiguationData":[OSD([subQ0]),TDD([makeQuery(id+"F0.imprint","IMPRINT",EDGE,{"disambiguationData":[TD([[makeQuery(id+"F0.imprint","INTERSECT",VERTEX,{"disambiguationData":[OD(1.0)],"derivedFrom":[subQ0,sQuery(id+"F0.wireOp",EDGE,"E6.1.0")]}),-1.0]])],"derivedFrom":subQ0})])],"isStart":false});}
            var Q1;
            {var subQ0=sQuery(id+"F0.wireOp",EDGE,"E6.1.0");Q1=makeQuery(id+"F1.opExtrude","CAP_EDGE",EDGE,{"disambiguationData":[OSD([subQ0]),TDD([makeQuery(id+"F0.imprint","IMPRINT",EDGE,{"disambiguationData":[TD([[makeQuery(id+"F0.imprint","INTERSECT",VERTEX,{"disambiguationData":[OD(1.0)],"derivedFrom":[sQuery(id+"F0.wireOp",EDGE,"E1"),subQ0]}),1.0]])],"derivedFrom":subQ0})])],"isStart":false});}
            var Q2;
            {var subQ0=sQuery(id+"F0.wireOp",EDGE,"E1");Q2=makeQuery(id+"F1.opExtrude","CAP_EDGE",EDGE,{"disambiguationData":[OSD([subQ0]),TDD([makeQuery(id+"F0.imprint","IMPRINT",EDGE,{"disambiguationData":[TD([[makeQuery(id+"F0.imprint","INTERSECT",VERTEX,{"disambiguationData":[OD(1.0)],"derivedFrom":[subQ0,sQuery(id+"F0.wireOp",EDGE,"E6.1.0")]}),-1.0]])],"derivedFrom":subQ0})])],"isStart":false});}
            var Q3;
            {var subQ0=sQuery(id+"F0.wireOp",EDGE,"E6.2.0");Q3=makeQuery(id+"F1.opExtrude","CAP_EDGE",EDGE,{"disambiguationData":[OSD([subQ0]),TDD([makeQuery(id+"F0.imprint","IMPRINT",EDGE,{"disambiguationData":[TD([[makeQuery(id+"F0.imprint","INTERSECT",VERTEX,{"disambiguationData":[OD(0.0)],"derivedFrom":[sQuery(id+"F0.wireOp",EDGE,"E1"),subQ0]}),-1.0]])],"derivedFrom":subQ0})])],"isStart":false});}
            var Q4;
            {var subQ0=sQuery(id+"F0.wireOp",EDGE,"E1");Q4=makeQuery(id+"F1.opExtrude","CAP_EDGE",EDGE,{"disambiguationData":[OSD([subQ0]),TDD([makeQuery(id+"F0.imprint","IMPRINT",EDGE,{"disambiguationData":[TD([[makeQuery(id+"F0.imprint","INTERSECT",VERTEX,{"disambiguationData":[OD(1.0)],"derivedFrom":[subQ0,sQuery(id+"F0.wireOp",EDGE,"E5")]}),1.0]])],"derivedFrom":subQ0})])],"isStart":false});}
            var Q5;
            {var subQ0=sQuery(id+"F0.wireOp",EDGE,"E5");Q5=makeQuery(id+"F1.opExtrude","CAP_EDGE",EDGE,{"disambiguationData":[OSD([subQ0]),TDD([makeQuery(id+"F0.imprint","IMPRINT",EDGE,{"disambiguationData":[TD([[makeQuery(id+"F0.imprint","INTERSECT",VERTEX,{"disambiguationData":[OD(1.0)],"derivedFrom":[sQuery(id+"F0.wireOp",EDGE,"E1"),subQ0]}),-1.0]])],"derivedFrom":subQ0})])],"isStart":false});}
            var Q6;
            {var subQ0=sQuery(id+"F0.wireOp",EDGE,"E3");Q6=makeQuery(id+"F1.opExtrude","CAP_EDGE",EDGE,{"disambiguationData":[OSD([subQ0]),TDD([makeQuery(id+"F0.imprint","IMPRINT",EDGE,{"disambiguationData":[TD([[makeQuery(id+"F0.imprint","INTERSECT",VERTEX,{"disambiguationData":[OD(0.0)],"derivedFrom":[subQ0,sQuery(id+"F0.wireOp",EDGE,"E5")]}),1.0]])],"derivedFrom":subQ0})])],"isStart":false});}
            var Q7;
            {var subQ0=sQuery(id+"F0.wireOp",EDGE,"E6.2.0");Q7=makeQuery(id+"F1.opExtrude","CAP_EDGE",EDGE,{"disambiguationData":[OSD([subQ0]),TDD([makeQuery(id+"F0.imprint","IMPRINT",EDGE,{"disambiguationData":[TD([[makeQuery(id+"F0.imprint","INTERSECT",VERTEX,{"disambiguationData":[OD(1.0)],"derivedFrom":[sQuery(id+"F0.wireOp",EDGE,"E1"),subQ0]}),1.0]])],"derivedFrom":subQ0})])],"isStart":false});}
            var Q8;
            {var subQ0=sQuery(id+"F0.wireOp",EDGE,"E6.1.0");Q8=makeQuery(id+"F1.opExtrude","CAP_EDGE",EDGE,{"disambiguationData":[OSD([subQ0]),TDD([makeQuery(id+"F0.imprint","IMPRINT",EDGE,{"disambiguationData":[TD([[makeQuery(id+"F0.imprint","INTERSECT",VERTEX,{"disambiguationData":[OD(0.0)],"derivedFrom":[sQuery(id+"F0.wireOp",EDGE,"E1"),subQ0]}),-1.0]])],"derivedFrom":subQ0})])],"isStart":false});}
            var Q9;
            {var subQ0=sQuery(id+"F0.wireOp",EDGE,"E1");Q9=makeQuery(id+"F1.opExtrude","CAP_EDGE",EDGE,{"disambiguationData":[OSD([subQ0]),TDD([makeQuery(id+"F0.imprint","IMPRINT",EDGE,{"disambiguationData":[TD([[makeQuery(id+"F0.imprint","INTERSECT",VERTEX,{"disambiguationData":[OD(0.0)],"derivedFrom":[subQ0,sQuery(id+"F0.wireOp",EDGE,"E5")]}),-1.0]])],"derivedFrom":subQ0})])],"isStart":false});}
            var Q10;
            {var subQ0=sQuery(id+"F0.wireOp",EDGE,"E5");Q10=makeQuery(id+"F1.opExtrude","CAP_EDGE",EDGE,{"disambiguationData":[OSD([subQ0]),TDD([makeQuery(id+"F0.imprint","IMPRINT",EDGE,{"disambiguationData":[TD([[makeQuery(id+"F0.imprint","INTERSECT",VERTEX,{"disambiguationData":[OD(0.0)],"derivedFrom":[sQuery(id+"F0.wireOp",EDGE,"E1"),subQ0]}),1.0]])],"derivedFrom":subQ0})])],"isStart":false});}
            var Q11;
            {var subQ0=sQuery(id+"F0.wireOp",EDGE,"E3");Q11=makeQuery(id+"F1.opExtrude","CAP_EDGE",EDGE,{"disambiguationData":[OSD([subQ0]),TDD([makeQuery(id+"F0.imprint","IMPRINT",EDGE,{"disambiguationData":[TD([[makeQuery(id+"F0.imprint","INTERSECT",VERTEX,{"disambiguationData":[OD(1.0)],"derivedFrom":[subQ0,sQuery(id+"F0.wireOp",EDGE,"E5")]}),-1.0]])],"derivedFrom":subQ0})])],"isStart":false});}
            var Q12;
            {var subQ0=sQuery(id+"F0.wireOp",EDGE,"E3");Q12=makeQuery(id+"F1.opExtrude","CAP_EDGE",EDGE,{"disambiguationData":[OSD([subQ0]),TDD([makeQuery(id+"F0.imprint","IMPRINT",EDGE,{"disambiguationData":[TD([[makeQuery(id+"F0.imprint","INTERSECT",VERTEX,{"disambiguationData":[OD(1.0)],"derivedFrom":[subQ0,sQuery(id+"F0.wireOp",EDGE,"E5")]}),-1.0]])],"derivedFrom":subQ0})])],"isStart":true});}
            var Q13;
            {var subQ0=sQuery(id+"F0.wireOp",EDGE,"E5");Q13=makeQuery(id+"F1.opExtrude","CAP_EDGE",EDGE,{"disambiguationData":[OSD([subQ0]),TDD([makeQuery(id+"F0.imprint","IMPRINT",EDGE,{"disambiguationData":[TD([[makeQuery(id+"F0.imprint","INTERSECT",VERTEX,{"disambiguationData":[OD(0.0)],"derivedFrom":[sQuery(id+"F0.wireOp",EDGE,"E1"),subQ0]}),1.0]])],"derivedFrom":subQ0})])],"isStart":true});}
            var Q14;
            {var subQ0=sQuery(id+"F0.wireOp",EDGE,"E1");Q14=makeQuery(id+"F1.opExtrude","CAP_EDGE",EDGE,{"disambiguationData":[OSD([subQ0]),TDD([makeQuery(id+"F0.imprint","IMPRINT",EDGE,{"disambiguationData":[TD([[makeQuery(id+"F0.imprint","INTERSECT",VERTEX,{"disambiguationData":[OD(0.0)],"derivedFrom":[subQ0,sQuery(id+"F0.wireOp",EDGE,"E5")]}),-1.0]])],"derivedFrom":subQ0})])],"isStart":true});}
            var Q15;
            {var subQ0=sQuery(id+"F0.wireOp",EDGE,"E6.1.0");Q15=makeQuery(id+"F1.opExtrude","CAP_EDGE",EDGE,{"disambiguationData":[OSD([subQ0]),TDD([makeQuery(id+"F0.imprint","IMPRINT",EDGE,{"disambiguationData":[TD([[makeQuery(id+"F0.imprint","INTERSECT",VERTEX,{"disambiguationData":[OD(0.0)],"derivedFrom":[sQuery(id+"F0.wireOp",EDGE,"E1"),subQ0]}),-1.0]])],"derivedFrom":subQ0})])],"isStart":true});}
            var Q16;
            {var subQ0=sQuery(id+"F0.wireOp",EDGE,"E3");Q16=makeQuery(id+"F1.opExtrude","CAP_EDGE",EDGE,{"disambiguationData":[OSD([subQ0]),TDD([makeQuery(id+"F0.imprint","IMPRINT",EDGE,{"disambiguationData":[TD([[makeQuery(id+"F0.imprint","INTERSECT",VERTEX,{"disambiguationData":[OD(1.0)],"derivedFrom":[subQ0,sQuery(id+"F0.wireOp",EDGE,"E6.1.0")]}),-1.0]])],"derivedFrom":subQ0})])],"isStart":true});}
            var Q17;
            {var subQ0=sQuery(id+"F0.wireOp",EDGE,"E6.1.0");Q17=makeQuery(id+"F1.opExtrude","CAP_EDGE",EDGE,{"disambiguationData":[OSD([subQ0]),TDD([makeQuery(id+"F0.imprint","IMPRINT",EDGE,{"disambiguationData":[TD([[makeQuery(id+"F0.imprint","INTERSECT",VERTEX,{"disambiguationData":[OD(1.0)],"derivedFrom":[sQuery(id+"F0.wireOp",EDGE,"E1"),subQ0]}),1.0]])],"derivedFrom":subQ0})])],"isStart":true});}
            var Q18;
            {var subQ0=sQuery(id+"F0.wireOp",EDGE,"E6.2.0");Q18=makeQuery(id+"F1.opExtrude","CAP_EDGE",EDGE,{"disambiguationData":[OSD([subQ0]),TDD([makeQuery(id+"F0.imprint","IMPRINT",EDGE,{"disambiguationData":[TD([[makeQuery(id+"F0.imprint","INTERSECT",VERTEX,{"disambiguationData":[OD(0.0)],"derivedFrom":[sQuery(id+"F0.wireOp",EDGE,"E1"),subQ0]}),-1.0]])],"derivedFrom":subQ0})])],"isStart":true});}
            var Q19;
            {var subQ0=sQuery(id+"F0.wireOp",EDGE,"E1");Q19=makeQuery(id+"F1.opExtrude","CAP_EDGE",EDGE,{"disambiguationData":[OSD([subQ0]),TDD([makeQuery(id+"F0.imprint","IMPRINT",EDGE,{"disambiguationData":[TD([[makeQuery(id+"F0.imprint","INTERSECT",VERTEX,{"disambiguationData":[OD(1.0)],"derivedFrom":[subQ0,sQuery(id+"F0.wireOp",EDGE,"E6.1.0")]}),-1.0]])],"derivedFrom":subQ0})])],"isStart":true});}
            var Q20;
            {var subQ0=sQuery(id+"F0.wireOp",EDGE,"E1");Q20=makeQuery(id+"F1.opExtrude","CAP_EDGE",EDGE,{"disambiguationData":[OSD([subQ0]),TDD([makeQuery(id+"F0.imprint","IMPRINT",EDGE,{"disambiguationData":[TD([[makeQuery(id+"F0.imprint","INTERSECT",VERTEX,{"disambiguationData":[OD(1.0)],"derivedFrom":[subQ0,sQuery(id+"F0.wireOp",EDGE,"E5")]}),1.0]])],"derivedFrom":subQ0})])],"isStart":true});}
            var Q21;
            {var subQ0=sQuery(id+"F0.wireOp",EDGE,"E5");Q21=makeQuery(id+"F1.opExtrude","CAP_EDGE",EDGE,{"disambiguationData":[OSD([subQ0]),TDD([makeQuery(id+"F0.imprint","IMPRINT",EDGE,{"disambiguationData":[TD([[makeQuery(id+"F0.imprint","INTERSECT",VERTEX,{"disambiguationData":[OD(1.0)],"derivedFrom":[sQuery(id+"F0.wireOp",EDGE,"E1"),subQ0]}),-1.0]])],"derivedFrom":subQ0})])],"isStart":true});}
            var Q22;
            {var subQ0=sQuery(id+"F0.wireOp",EDGE,"E3");Q22=makeQuery(id+"F1.opExtrude","CAP_EDGE",EDGE,{"disambiguationData":[OSD([subQ0]),TDD([makeQuery(id+"F0.imprint","IMPRINT",EDGE,{"disambiguationData":[TD([[makeQuery(id+"F0.imprint","INTERSECT",VERTEX,{"disambiguationData":[OD(0.0)],"derivedFrom":[subQ0,sQuery(id+"F0.wireOp",EDGE,"E5")]}),1.0]])],"derivedFrom":subQ0})])],"isStart":true});}
            var Q23;
            {var subQ0=sQuery(id+"F0.wireOp",EDGE,"E6.2.0");Q23=makeQuery(id+"F1.opExtrude","CAP_EDGE",EDGE,{"disambiguationData":[OSD([subQ0]),TDD([makeQuery(id+"F0.imprint","IMPRINT",EDGE,{"disambiguationData":[TD([[makeQuery(id+"F0.imprint","INTERSECT",VERTEX,{"disambiguationData":[OD(1.0)],"derivedFrom":[sQuery(id+"F0.wireOp",EDGE,"E1"),subQ0]}),1.0]])],"derivedFrom":subQ0})])],"isStart":true});}
            var Q24;
            {var subQ0=sQuery(id+"F0.wireOp",EDGE,"E1");Q24=makeQuery(id+"F1.opExtrude","CAP_EDGE",EDGE,{"disambiguationData":[OSD([subQ0]),TDD([makeQuery(id+"F0.imprint","IMPRINT",EDGE,{"disambiguationData":[TD([[makeQuery(id+"F0.imprint","INTERSECT",VERTEX,{"disambiguationData":[OD(0.0)],"derivedFrom":[subQ0,sQuery(id+"F0.wireOp",EDGE,"E5")]}),1.0]])],"derivedFrom":subQ0})])],"isStart":false});}
            var Q25;
            {var subQ0=sQuery(id+"F0.wireOp",EDGE,"E1");Q25=makeQuery(id+"F1.opExtrude","CAP_EDGE",EDGE,{"disambiguationData":[OSD([subQ0]),TDD([makeQuery(id+"F0.imprint","IMPRINT",EDGE,{"disambiguationData":[TD([[makeQuery(id+"F0.imprint","INTERSECT",VERTEX,{"disambiguationData":[OD(0.0)],"derivedFrom":[subQ0,sQuery(id+"F0.wireOp",EDGE,"E5")]}),1.0]])],"derivedFrom":subQ0})])],"isStart":true});}
            var Q26;
            {var subQ0=sQuery(id+"F0.wireOp",EDGE,"E5");Q26=makeQuery(id+"F1.opExtrude","CAP_EDGE",EDGE,{"disambiguationData":[OSD([subQ0]),TDD([makeQuery(id+"F0.imprint","IMPRINT",EDGE,{"disambiguationData":[TD([[makeQuery(id+"F0.imprint","INTERSECT",VERTEX,{"disambiguationData":[OD(0.0)],"derivedFrom":[sQuery(id+"F0.wireOp",EDGE,"E1"),subQ0]}),-1.0]])],"derivedFrom":subQ0})])],"isStart":false});}
            var Q27;
            {var subQ0=sQuery(id+"F0.wireOp",EDGE,"e3311fa9-2675-4763-9959-c69614a33db8.1.3.0");Q27=makeQuery(id+"F1.opExtrude","CAP_EDGE",EDGE,{"disambiguationData":[OSD([subQ0]),TDD([makeQuery(id+"F0.imprint","IMPRINT",EDGE,{"disambiguationData":[TD([[makeQuery(id+"F0.imprint","INTERSECT",VERTEX,{"disambiguationData":[OD(0.0)],"derivedFrom":[sQuery(id+"F0.wireOp",EDGE,"E1"),subQ0]}),1.0]])],"derivedFrom":subQ0})])],"isStart":false});}
            var Q28;
            {var subQ0=sQuery(id+"F0.wireOp",EDGE,"E5");Q28=makeQuery(id+"F1.opExtrude","CAP_EDGE",EDGE,{"disambiguationData":[OSD([subQ0]),TDD([makeQuery(id+"F0.imprint","IMPRINT",EDGE,{"disambiguationData":[TD([[makeQuery(id+"F0.imprint","INTERSECT",VERTEX,{"disambiguationData":[OD(0.0)],"derivedFrom":[sQuery(id+"F0.wireOp",EDGE,"E1"),subQ0]}),-1.0]])],"derivedFrom":subQ0})])],"isStart":true});}
            var Q29;
            {var subQ0=sQuery(id+"F0.wireOp",EDGE,"e3311fa9-2675-4763-9959-c69614a33db8.1.3.0");Q29=makeQuery(id+"F1.opExtrude","CAP_EDGE",EDGE,{"disambiguationData":[OSD([subQ0]),TDD([makeQuery(id+"F0.imprint","IMPRINT",EDGE,{"disambiguationData":[TD([[makeQuery(id+"F0.imprint","INTERSECT",VERTEX,{"disambiguationData":[OD(0.0)],"derivedFrom":[sQuery(id+"F0.wireOp",EDGE,"E1"),subQ0]}),1.0]])],"derivedFrom":subQ0})])],"isStart":true});}
            var Q30;
            {var subQ0=sQuery(id+"F0.wireOp",EDGE,"E1");Q30=makeQuery(id+"F1.opExtrude","CAP_EDGE",EDGE,{"disambiguationData":[OSD([subQ0]),TDD([makeQuery(id+"F0.imprint","IMPRINT",EDGE,{"disambiguationData":[TD([[makeQuery(id+"F0.imprint","INTERSECT",VERTEX,{"disambiguationData":[OD(1.0)],"derivedFrom":[subQ0,sQuery(id+"F0.wireOp",EDGE,"E6.2.0")]}),-1.0]])],"derivedFrom":subQ0})])],"isStart":false});}
            var Q31;
            {var subQ0=sQuery(id+"F0.wireOp",EDGE,"e3311fa9-2675-4763-9959-c69614a33db8.1.3.0");Q31=makeQuery(id+"F1.opExtrude","CAP_EDGE",EDGE,{"disambiguationData":[OSD([subQ0]),TDD([makeQuery(id+"F0.imprint","IMPRINT",EDGE,{"disambiguationData":[TD([[makeQuery(id+"F0.imprint","INTERSECT",VERTEX,{"disambiguationData":[OD(1.0)],"derivedFrom":[sQuery(id+"F0.wireOp",EDGE,"E1"),subQ0]}),-1.0]])],"derivedFrom":subQ0})])],"isStart":false});}
            var Q32;
            {var subQ0=sQuery(id+"F0.wireOp",EDGE,"E3");Q32=makeQuery(id+"F1.opExtrude","CAP_EDGE",EDGE,{"disambiguationData":[OSD([subQ0]),TDD([makeQuery(id+"F0.imprint","IMPRINT",EDGE,{"disambiguationData":[TD([[makeQuery(id+"F0.imprint","INTERSECT",VERTEX,{"disambiguationData":[OD(1.0)],"derivedFrom":[subQ0,sQuery(id+"F0.wireOp",EDGE,"E6.2.0")]}),-1.0]])],"derivedFrom":subQ0})])],"isStart":false});}
            var Q33;
            {var subQ0=sQuery(id+"F0.wireOp",EDGE,"E1");Q33=makeQuery(id+"F1.opExtrude","CAP_EDGE",EDGE,{"disambiguationData":[OSD([subQ0]),TDD([makeQuery(id+"F0.imprint","IMPRINT",EDGE,{"disambiguationData":[TD([[makeQuery(id+"F0.imprint","INTERSECT",VERTEX,{"disambiguationData":[OD(1.0)],"derivedFrom":[subQ0,sQuery(id+"F0.wireOp",EDGE,"E5")]}),-1.0]])],"derivedFrom":subQ0})])],"isStart":false});}
            var Q34;
            {var subQ0=sQuery(id+"F0.wireOp",EDGE,"E5");Q34=makeQuery(id+"F1.opExtrude","CAP_EDGE",EDGE,{"disambiguationData":[OSD([subQ0]),TDD([makeQuery(id+"F0.imprint","IMPRINT",EDGE,{"disambiguationData":[TD([[makeQuery(id+"F0.imprint","INTERSECT",VERTEX,{"disambiguationData":[OD(1.0)],"derivedFrom":[sQuery(id+"F0.wireOp",EDGE,"E1"),subQ0]}),1.0]])],"derivedFrom":subQ0})])],"isStart":false});}
            var Q35;
            {var subQ0=sQuery(id+"F0.wireOp",EDGE,"E1");Q35=makeQuery(id+"F1.opExtrude","CAP_EDGE",EDGE,{"disambiguationData":[OSD([subQ0]),TDD([makeQuery(id+"F0.imprint","IMPRINT",EDGE,{"disambiguationData":[TD([[makeQuery(id+"F0.imprint","INTERSECT",VERTEX,{"disambiguationData":[OD(1.0)],"derivedFrom":[subQ0,sQuery(id+"F0.wireOp",EDGE,"E5")]}),-1.0]])],"derivedFrom":subQ0})])],"isStart":true});}
            var Q36;
            {var subQ0=sQuery(id+"F0.wireOp",EDGE,"E5");Q36=makeQuery(id+"F1.opExtrude","CAP_EDGE",EDGE,{"disambiguationData":[OSD([subQ0]),TDD([makeQuery(id+"F0.imprint","IMPRINT",EDGE,{"disambiguationData":[TD([[makeQuery(id+"F0.imprint","INTERSECT",VERTEX,{"disambiguationData":[OD(1.0)],"derivedFrom":[sQuery(id+"F0.wireOp",EDGE,"E1"),subQ0]}),1.0]])],"derivedFrom":subQ0})])],"isStart":true});}
            var Q37;
            {var subQ0=sQuery(id+"F0.wireOp",EDGE,"E7.1.3.0");Q37=makeQuery(id+"F1.opExtrude","CAP_EDGE",EDGE,{"disambiguationData":[OSD([subQ0]),TDD([makeQuery(id+"F0.imprint","IMPRINT",EDGE,{"disambiguationData":[TD([[makeQuery(id+"F0.imprint","INTERSECT",VERTEX,{"disambiguationData":[OD(0.0)],"derivedFrom":[sQuery(id+"F0.wireOp",EDGE,"E1"),subQ0]}),-1.0]])],"derivedFrom":subQ0})])],"isStart":false});}
            var Q38;
            {var subQ0=sQuery(id+"F0.wireOp",EDGE,"E7.1.4.0");Q38=makeQuery(id+"F1.opExtrude","CAP_EDGE",EDGE,{"disambiguationData":[OSD([subQ0]),TDD([makeQuery(id+"F0.imprint","IMPRINT",EDGE,{"disambiguationData":[TD([[makeQuery(id+"F0.imprint","INTERSECT",VERTEX,{"disambiguationData":[OD(1.0)],"derivedFrom":[sQuery(id+"F0.wireOp",EDGE,"E1"),subQ0]}),-1.0]])],"derivedFrom":subQ0})])],"isStart":false});}
            var Q39;
            {var subQ0=sQuery(id+"F0.wireOp",EDGE,"E3");Q39=makeQuery(id+"F1.opExtrude","CAP_EDGE",EDGE,{"disambiguationData":[OSD([subQ0]),TDD([makeQuery(id+"F0.imprint","IMPRINT",EDGE,{"disambiguationData":[TD([[makeQuery(id+"F0.imprint","INTERSECT",VERTEX,{"disambiguationData":[OD(1.0)],"derivedFrom":[subQ0,sQuery(id+"F0.wireOp",EDGE,"E7.1.3.0")]}),-1.0]])],"derivedFrom":subQ0})])],"isStart":false});}
            var Q40;
            {var subQ0=sQuery(id+"F0.wireOp",EDGE,"E7.1.3.0");Q40=makeQuery(id+"F1.opExtrude","CAP_EDGE",EDGE,{"disambiguationData":[OSD([subQ0]),TDD([makeQuery(id+"F0.imprint","IMPRINT",EDGE,{"disambiguationData":[TD([[makeQuery(id+"F0.imprint","INTERSECT",VERTEX,{"disambiguationData":[OD(1.0)],"derivedFrom":[sQuery(id+"F0.wireOp",EDGE,"E1"),subQ0]}),1.0]])],"derivedFrom":subQ0})])],"isStart":false});}
            var Q41;
            {var subQ0=sQuery(id+"F0.wireOp",EDGE,"E1");Q41=makeQuery(id+"F1.opExtrude","CAP_EDGE",EDGE,{"disambiguationData":[OSD([subQ0]),TDD([makeQuery(id+"F0.imprint","IMPRINT",EDGE,{"disambiguationData":[TD([[makeQuery(id+"F0.imprint","INTERSECT",VERTEX,{"disambiguationData":[OD(1.0)],"derivedFrom":[subQ0,sQuery(id+"F0.wireOp",EDGE,"E7.1.3.0")]}),-1.0]])],"derivedFrom":subQ0})])],"isStart":false});}
            var Q42;
            {var subQ0=sQuery(id+"F0.wireOp",EDGE,"E7.1.4.0");Q42=makeQuery(id+"F1.opExtrude","CAP_EDGE",EDGE,{"disambiguationData":[OSD([subQ0]),TDD([makeQuery(id+"F0.imprint","IMPRINT",EDGE,{"disambiguationData":[TD([[makeQuery(id+"F0.imprint","INTERSECT",VERTEX,{"disambiguationData":[OD(0.0)],"derivedFrom":[sQuery(id+"F0.wireOp",EDGE,"E1"),subQ0]}),1.0]])],"derivedFrom":subQ0})])],"isStart":false});}
            var Q43;
            {var subQ0=sQuery(id+"F0.wireOp",EDGE,"E1");Q43=makeQuery(id+"F1.opExtrude","CAP_EDGE",EDGE,{"disambiguationData":[OSD([subQ0]),TDD([makeQuery(id+"F0.imprint","IMPRINT",EDGE,{"disambiguationData":[TD([[makeQuery(id+"F0.imprint","INTERSECT",VERTEX,{"disambiguationData":[OD(1.0)],"derivedFrom":[subQ0,sQuery(id+"F0.wireOp",EDGE,"E6.2.0")]}),-1.0]])],"derivedFrom":subQ0})])],"isStart":true});}
            var Q44;
            {var subQ0=sQuery(id+"F0.wireOp",EDGE,"E1");Q44=makeQuery(id+"F1.opExtrude","CAP_EDGE",EDGE,{"disambiguationData":[OSD([subQ0]),TDD([makeQuery(id+"F0.imprint","IMPRINT",EDGE,{"disambiguationData":[TD([[makeQuery(id+"F0.imprint","INTERSECT",VERTEX,{"disambiguationData":[OD(1.0)],"derivedFrom":[subQ0,sQuery(id+"F0.wireOp",EDGE,"E7.1.3.0")]}),-1.0]])],"derivedFrom":subQ0})])],"isStart":true});}
            var Q45;
            {var subQ0=sQuery(id+"F0.wireOp",EDGE,"E7.1.4.0");Q45=makeQuery(id+"F1.opExtrude","CAP_EDGE",EDGE,{"disambiguationData":[OSD([subQ0]),TDD([makeQuery(id+"F0.imprint","IMPRINT",EDGE,{"disambiguationData":[TD([[makeQuery(id+"F0.imprint","INTERSECT",VERTEX,{"disambiguationData":[OD(1.0)],"derivedFrom":[sQuery(id+"F0.wireOp",EDGE,"E1"),subQ0]}),-1.0]])],"derivedFrom":subQ0})])],"isStart":true});}
            var Q46;
            {var subQ0=sQuery(id+"F0.wireOp",EDGE,"E7.1.3.0");Q46=makeQuery(id+"F1.opExtrude","CAP_EDGE",EDGE,{"disambiguationData":[OSD([subQ0]),TDD([makeQuery(id+"F0.imprint","IMPRINT",EDGE,{"disambiguationData":[TD([[makeQuery(id+"F0.imprint","INTERSECT",VERTEX,{"disambiguationData":[OD(1.0)],"derivedFrom":[sQuery(id+"F0.wireOp",EDGE,"E1"),subQ0]}),1.0]])],"derivedFrom":subQ0})])],"isStart":true});}
            var Q47;
            {var subQ0=sQuery(id+"F0.wireOp",EDGE,"E3");Q47=makeQuery(id+"F1.opExtrude","CAP_EDGE",EDGE,{"disambiguationData":[OSD([subQ0]),TDD([makeQuery(id+"F0.imprint","IMPRINT",EDGE,{"disambiguationData":[TD([[makeQuery(id+"F0.imprint","INTERSECT",VERTEX,{"disambiguationData":[OD(1.0)],"derivedFrom":[subQ0,sQuery(id+"F0.wireOp",EDGE,"E7.1.3.0")]}),-1.0]])],"derivedFrom":subQ0})])],"isStart":true});}
            var Q48;
            {var subQ0=sQuery(id+"F0.wireOp",EDGE,"E7.1.3.0");Q48=makeQuery(id+"F1.opExtrude","CAP_EDGE",EDGE,{"disambiguationData":[OSD([subQ0]),TDD([makeQuery(id+"F0.imprint","IMPRINT",EDGE,{"disambiguationData":[TD([[makeQuery(id+"F0.imprint","INTERSECT",VERTEX,{"disambiguationData":[OD(0.0)],"derivedFrom":[sQuery(id+"F0.wireOp",EDGE,"E1"),subQ0]}),-1.0]])],"derivedFrom":subQ0})])],"isStart":true});}
            var Q49;
            {var subQ0=sQuery(id+"F0.wireOp",EDGE,"E7.1.4.0");Q49=makeQuery(id+"F1.opExtrude","CAP_EDGE",EDGE,{"disambiguationData":[OSD([subQ0]),TDD([makeQuery(id+"F0.imprint","IMPRINT",EDGE,{"disambiguationData":[TD([[makeQuery(id+"F0.imprint","INTERSECT",VERTEX,{"disambiguationData":[OD(0.0)],"derivedFrom":[sQuery(id+"F0.wireOp",EDGE,"E1"),subQ0]}),1.0]])],"derivedFrom":subQ0})])],"isStart":true});}
            fillet(context, id + "F3", {"entities" : qUnion([Q0, Q1, Q2, Q3, Q4, Q5, Q6, Q7, Q8, Q9, Q10, Q11, Q12, Q13, Q14, Q15, Q16, Q17, Q18, Q19, Q20, Q21, Q22, Q23, Q24, Q25, Q26, Q27, Q28, Q29, Q30, Q31, Q32, Q33, Q34, Q35, Q36, Q37, Q38, Q39, Q40, Q41, Q42, Q43, Q44, Q45, Q46, Q47, Q48, Q49]), "radius" : 1 * mm, "tangentPropagation" : true, "allowEdgeOverflow" : false});
        }
    });
